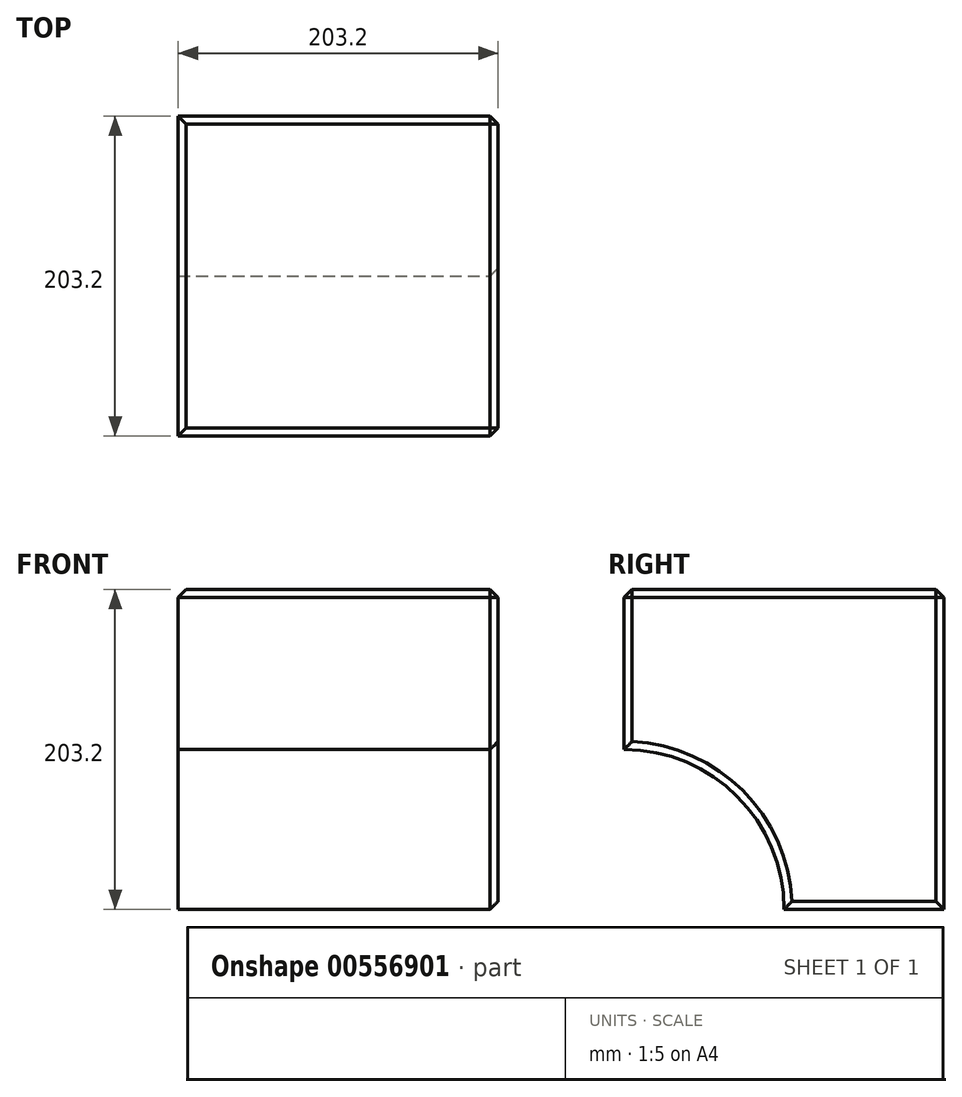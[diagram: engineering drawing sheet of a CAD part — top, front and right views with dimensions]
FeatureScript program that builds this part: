
annotation { "Feature Type Name" : "Feature", "Feature Type Description" : "" }
export const myFeature = defineFeature(function(context is Context, id is Id, definition is map)
    precondition{}
    {
        {
            var Q0;
            Q0=qCreatedBy(makeId("Right.planeOp"),FACE);
            var sketch = newSketch(context, id + "F0", { "sketchPlane" : qUnion([Q0])});
            skLineSegment(sketch, "E0.bottom", {"start": v(-101.6, -101.6) * mm, "end": v(101.6, -101.6) * mm});
            skLineSegment(sketch, "E0.top", {"start": v(-101.6, 101.6) * mm, "end": v(101.6, 101.6) * mm});
            skLineSegment(sketch, "E0.left", {"start": v(-101.6, -101.6) * mm, "end": v(-101.6, 101.6) * mm});
            skLineSegment(sketch, "E0.right", {"start": v(101.6, -101.6) * mm, "end": v(101.6, 101.6) * mm});
            skPoint(sketch, "E0.middle", {"position": v(0, 0) * mm});
            skSolve(sketch);
        }
        {
            var Q0;
            Q0 = qSketchRegion(id + "F0", true);
            extrude(context, id + "F1", {"entities" : qUnion([Q0]), "endBound" : BoundingType.SYMMETRIC, "depth" : 203.2 * mm, "offsetDistance" : 25.4 * mm});
        }
        {
            var Q0;
            Q0=makeQuery(id+"F1.opExtrude","CAP_FACE",FACE,{"disambiguationData":[OSD([sQuery(id+"F0.wireOp",EDGE,"E0.bottom"),sQuery(id+"F0.wireOp",EDGE,"E0.top"),sQuery(id+"F0.wireOp",EDGE,"E0.left"),sQuery(id+"F0.wireOp",EDGE,"E0.right")])],"isStart":false});
            var sketch = newSketch(context, id + "F2", { "sketchPlane" : qUnion([Q0])});
            skCircle(sketch, "E1", {"center": v(-101.6, -101.6) * mm, "radius": 101.6 * mm});
            skSolve(sketch);
        }
        {
            var Q0;
            Q0 = qSketchRegion(id + "F2", true);
            extrude(context, id + "F3", {"entities" : qUnion([Q0]), "operationType" : NewBodyOperationType.REMOVE, "endBound" : BoundingType.THROUGH_ALL, "oppositeDirection" : true, "depth" : 25.4 * mm, "offsetDistance" : 25.4 * mm});
        }
        {
            var Q0;
            Q0=makeQuery(id+"F1.opExtrude","CAP_FACE",FACE,{"disambiguationData":[OSD([sQuery(id+"F0.wireOp",EDGE,"E0.bottom"),sQuery(id+"F0.wireOp",EDGE,"E0.top"),sQuery(id+"F0.wireOp",EDGE,"E0.left"),sQuery(id+"F0.wireOp",EDGE,"E0.right")])],"isStart":false});
            var Q1;
            Q1=makeQuery(id+"F1.opExtrude","SWEPT_FACE",FACE,{"disambiguationData":[OSD([sQuery(id+"F0.wireOp",EDGE,"E0.top")])]});
            chamfer(context, id + "F4", {"entities" : qUnion([Q0, Q1]), "width" : 5.08 * mm, "tangentPropagation" : true});
        }
    });
